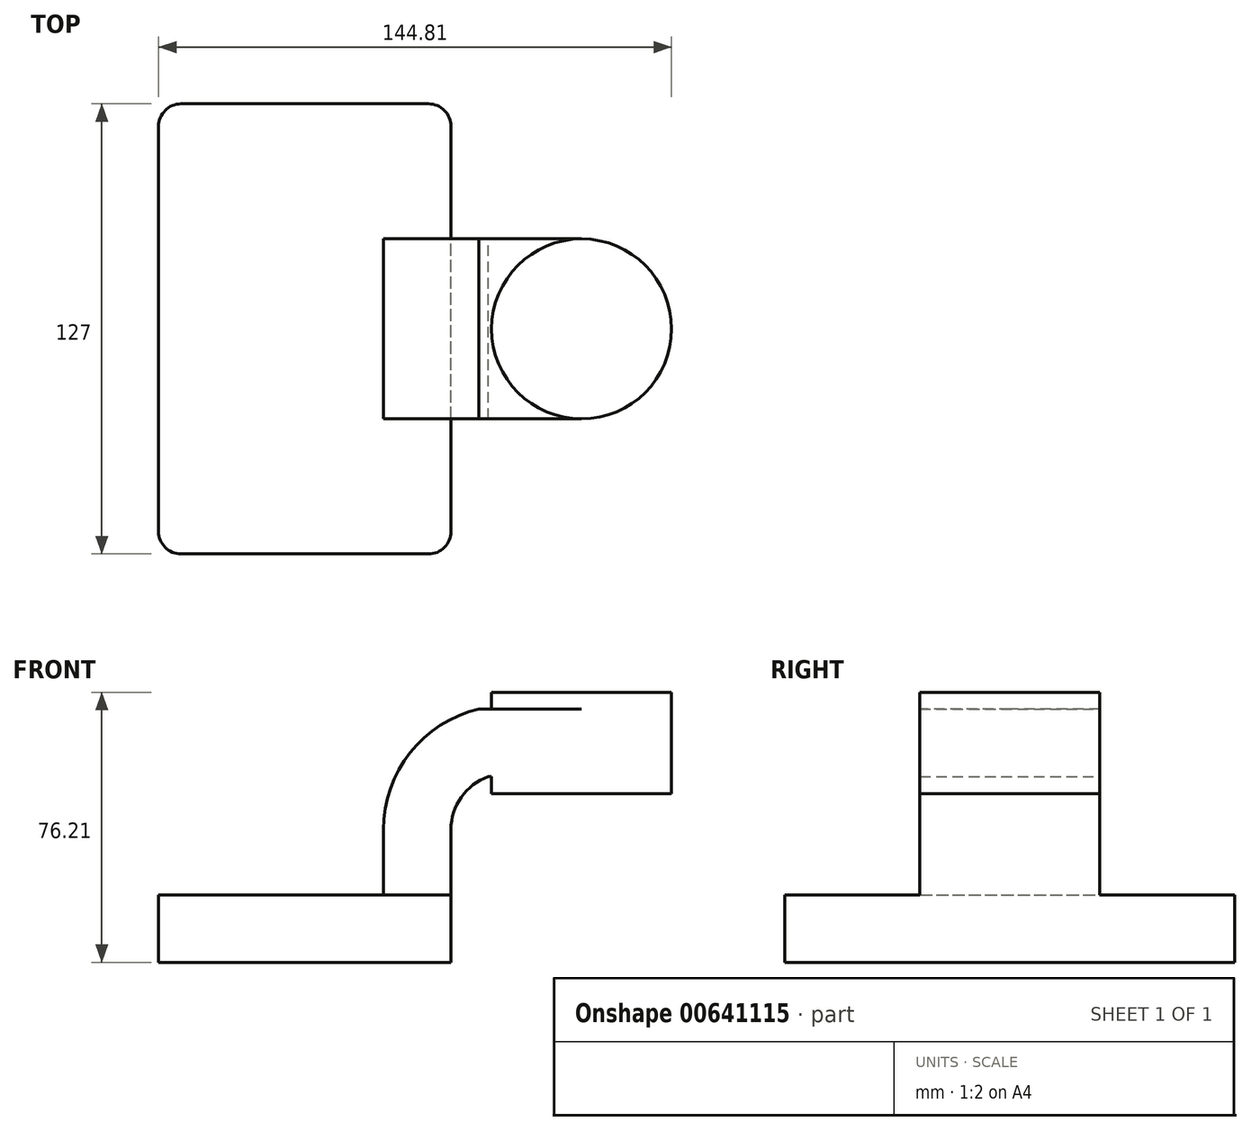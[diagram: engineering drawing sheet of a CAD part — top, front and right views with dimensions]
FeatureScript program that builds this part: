
annotation { "Feature Type Name" : "Feature", "Feature Type Description" : "" }
export const myFeature = defineFeature(function(context is Context, id is Id, definition is map)
    precondition{}
    {
        {
            var Q0;
            Q0=qCreatedBy(makeId("Front.planeOp"),FACE);
            var sketch = newSketch(context, id + "F0", { "sketchPlane" : qUnion([Q0])});
            skLineSegment(sketch, "E0.bottom", {"start": v(41.28, 9.53) * mm, "end": v(-41.28, 9.53) * mm});
            skLineSegment(sketch, "E0.top", {"start": v(41.28, -9.53) * mm, "end": v(-41.28, -9.53) * mm});
            skLineSegment(sketch, "E0.left", {"start": v(41.28, 9.53) * mm, "end": v(41.28, -9.53) * mm});
            skLineSegment(sketch, "E0.right", {"start": v(-41.28, 9.53) * mm, "end": v(-41.28, -9.53) * mm});
            skPoint(sketch, "E0.middle", {"position": v(0, 0) * mm});
            skLineSegment(sketch, "E1.bottom", {"start": v(103.54, 38.1) * mm, "end": v(52.74, 38.1) * mm});
            skLineSegment(sketch, "E1.top", {"start": v(103.54, 66.68) * mm, "end": v(52.74, 66.68) * mm});
            skLineSegment(sketch, "E1.left", {"start": v(103.54, 38.1) * mm, "end": v(103.54, 66.68) * mm});
            skLineSegment(sketch, "E1.right", {"start": v(52.74, 38.1) * mm, "end": v(52.74, 66.68) * mm});
            skPoint(sketch, "E1.middle", {"position": v(78.14, 52.39) * mm});
            skLineSegment(sketch, "E2", {"start": v(41.28, 9.53) * mm, "end": v(41.28, 27.93) * mm});
            skArc(sketch, "E3", {"start": v(41.27, 27.93) * mm, "mid": v(44.17, 37.07) * mm, "end": v(51.79, 42.88) * mm});
            skLineSegment(sketch, "E4", {"start": v(51.79, 42.88) * mm, "end": v(77.1, 42.88) * mm});
            skLineSegment(sketch, "E5.0", {"start": v(49.13, 61.93) * mm, "end": v(78.14, 61.93) * mm});
            skArc(sketch, "E5.1", {"start": v(22.22, 27.93) * mm, "mid": v(29.76, 49.6) * mm, "end": v(49.13, 61.93) * mm});
            skLineSegment(sketch, "E5.2", {"start": v(22.22, 9.53) * mm, "end": v(22.22, 27.93) * mm});
            skLineSegment(sketch, "E6", {"start": v(78.14, 38.1) * mm, "end": v(78.14, 66.67) * mm});
            skFitSpline(sketch, "E7", {"points": [v(-41.28, 9.53) * mm, v(49.13, 61.93) * mm], "startDerivative": vector(3.8, 111.1) * mm, "endDerivative": vector(106.93, 5.78) * mm});
            skSolve(sketch);
        }
        {
            var Q0;
            Q0=makeQuery(id+"F0.imprint","IMPRINT",FACE,{"disambiguationData":[TD([[makeQuery(id+"F0.imprint","IMPRINT",EDGE,{"derivedFrom":sQuery(id+"F0.wireOp",EDGE,"E0.top")}),-1.0]])]});
            extrude(context, id + "F1", {"entities" : qUnion([Q0]), "endBound" : BoundingType.SYMMETRIC, "depth" : 127 * mm, "offsetDistance" : 25.4 * mm});
        }
        {
            var Q0;
            {var subQ1=sQuery(id+"F0.wireOp",EDGE,"E2");Q0=makeQuery(id+"F0.imprint","IMPRINT",FACE,{"disambiguationData":[TD([[makeQuery(id+"F0.imprint","IMPRINT",EDGE,{"derivedFrom":subQ1}),1.0]])]});}
            extrude(context, id + "F2", {"entities" : qUnion([Q0]), "operationType" : NewBodyOperationType.ADD, "endBound" : BoundingType.SYMMETRIC, "depth" : 50.8 * mm, "offsetDistance" : 25.4 * mm});
        }
        {
            var Q0;
            Q0=makeQuery(id+"F0.imprint","IMPRINT",FACE,{"disambiguationData":[TD([[makeQuery(id+"F0.imprint","IMPRINT",EDGE,{"derivedFrom":sQuery(id+"F0.wireOp",EDGE,"E5.1")}),1.0]])]});
            extrude(context, id + "F3", {"entities" : qUnion([Q0]), "operationType" : NewBodyOperationType.ADD, "endBound" : BoundingType.SYMMETRIC, "depth" : 15.88 * mm, "offsetDistance" : 25.4 * mm});
        }
        {
            var Q0;
            {var subQ3=sQuery(id+"F0.wireOp",EDGE,"E1.right");var subQ5=sQuery(id+"F0.wireOp",EDGE,"E1.bottom");var subQ6=makeQuery(id+"F0.imprint","INTERSECT",VERTEX,{"derivedFrom":[subQ5,subQ3]});Q0=makeQuery(id+"F0.imprint","IMPRINT",FACE,{"disambiguationData":[TD([[makeQuery(id+"F0.imprint","IMPRINT",EDGE,{"disambiguationData":[TD([[subQ6,1.0]])],"derivedFrom":subQ5}),-1.0]])]});}
            extrude(context, id + "F4", {"entities" : qUnion([Q0]), "operationType" : NewBodyOperationType.ADD, "endBound" : BoundingType.SYMMETRIC, "depth" : 50.8 * mm, "offsetDistance" : 25.4 * mm});
        }
        {
            var Q0;
            {var subQ0=sQuery(id+"F0.wireOp",EDGE,"E1.left");Q0=makeQuery(id+"F0.imprint","IMPRINT",FACE,{"disambiguationData":[TD([[makeQuery(id+"F0.imprint","IMPRINT",EDGE,{"derivedFrom":subQ0}),1.0]])]});}
            var Q1;
            Q1=sQuery(id+"F0.wireOp",EDGE,"E6");
            revolve(context, id + "F5", {"operationType" : NewBodyOperationType.ADD, "entities" : qUnion([Q0]), "axis" : qUnion([Q1]), "revolveType" : RevolveType.FULL});
        }
        {
            var Q0;
            Q0=makeQuery(id+"F1.opExtrude","CAP_EDGE",EDGE,{"disambiguationData":[OSD([sQuery(id+"F0.wireOp",EDGE,"E0.left")])],"isStart":false});
            var Q1;
            Q1=makeQuery(id+"F1.opExtrude","CAP_EDGE",EDGE,{"disambiguationData":[OSD([sQuery(id+"F0.wireOp",EDGE,"E0.right")])],"isStart":false});
            var Q2;
            Q2=makeQuery(id+"F1.opExtrude","CAP_EDGE",EDGE,{"disambiguationData":[OSD([sQuery(id+"F0.wireOp",EDGE,"E0.right")])],"isStart":true});
            var Q3;
            Q3=makeQuery(id+"F1.opExtrude","CAP_EDGE",EDGE,{"disambiguationData":[OSD([sQuery(id+"F0.wireOp",EDGE,"E0.left")])],"isStart":true});
            fillet(context, id + "F6", {"entities" : qUnion([Q0, Q1, Q2, Q3]), "radius" : 6.35 * mm, "tangentPropagation" : true, "allowEdgeOverflow" : false});
        }
    });
